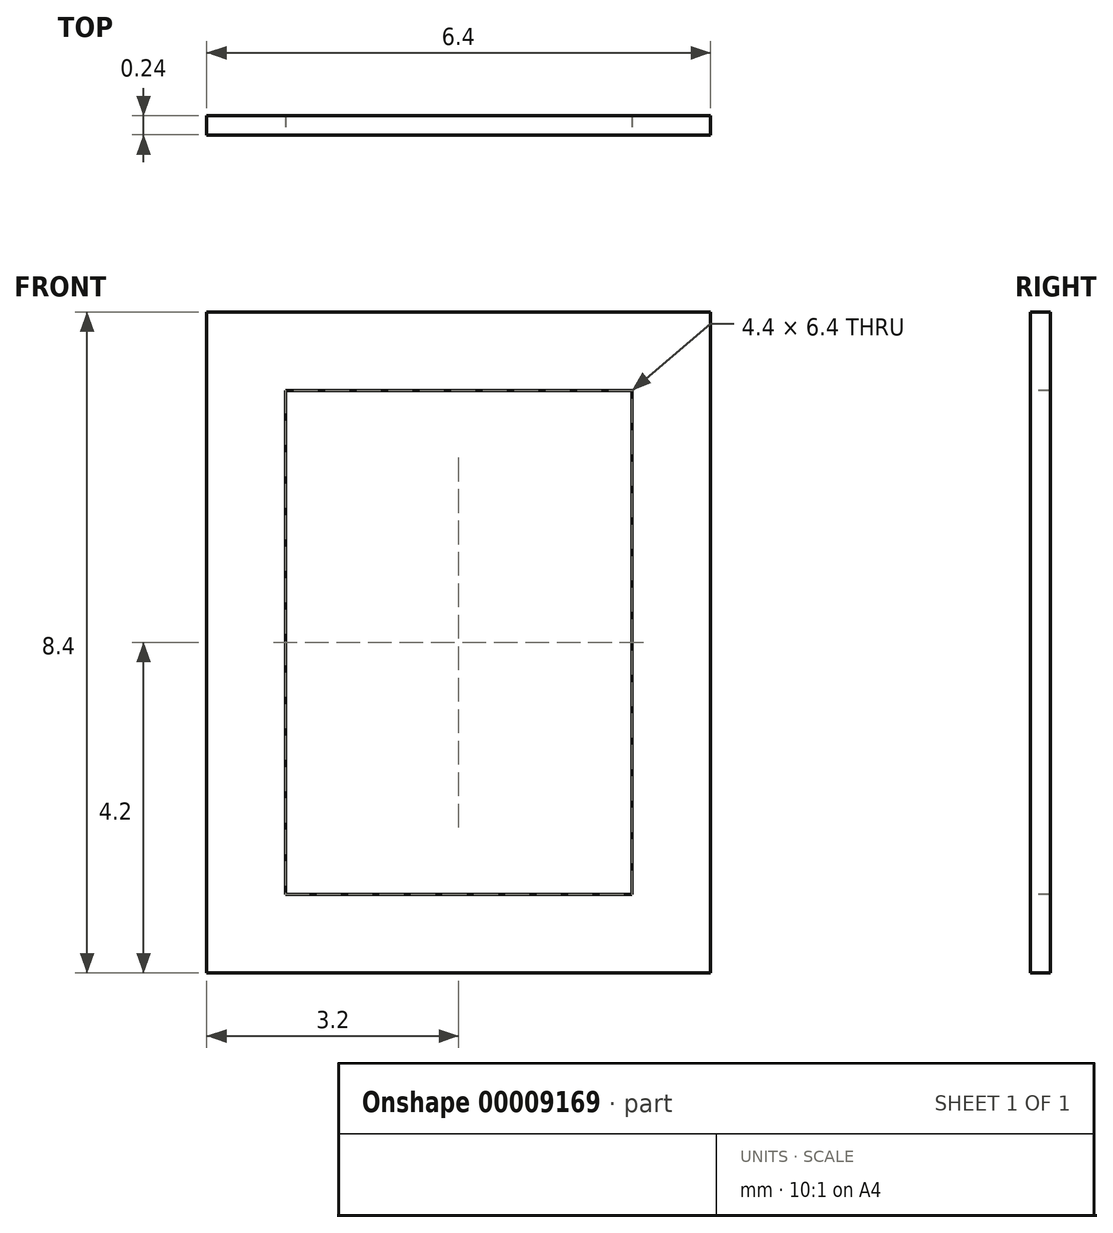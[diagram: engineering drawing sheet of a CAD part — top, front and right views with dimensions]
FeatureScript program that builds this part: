
annotation { "Feature Type Name" : "Feature", "Feature Type Description" : "" }
export const myFeature = defineFeature(function(context is Context, id is Id, definition is map)
    precondition{}
    {
        {
            var Q0;
            Q0=qCreatedBy(makeId("Top.planeOp"),FACE);
            var sketch = newSketch(context, id + "F0", { "sketchPlane" : qUnion([Q0])});
            skLineSegment(sketch, "E0.rect.bottom", {"start": v(3.2, 0.12) * mm, "end": v(-3.2, 0.13) * mm});
            skLineSegment(sketch, "E0.rect.top", {"start": v(3.2, -0.13) * mm, "end": v(-3.2, -0.12) * mm});
            skLineSegment(sketch, "E0.rect.left", {"start": v(3.2, 0.12) * mm, "end": v(3.2, -0.13) * mm});
            skLineSegment(sketch, "E0.rect.right", {"start": v(-3.2, 0.13) * mm, "end": v(-3.2, -0.12) * mm});
            skPoint(sketch, "E0.rect.middle", {"position": v(0, 0) * mm});
            skSolve(sketch);
        }
        {
            var Q0;
            Q0=makeQuery(id+"F0.imprint","IMPRINT",FACE,{"disambiguationData":[TD([[makeQuery(id+"F0.imprint","IMPRINT",EDGE,{"derivedFrom":sQuery(id+"F0.wireOp",EDGE,"E0.rect.bottom")}),1.0]])]});
            extrude(context, id + "F1", {"entities" : qUnion([Q0]), "depth" : 8.4 * mm});
        }
        {
            var Q0;
            Q0=makeQuery(id+"F1.opExtrude","SWEPT_FACE",FACE,{"disambiguationData":[OSD([sQuery(id+"F0.wireOp",EDGE,"E0.rect.top")])]});
            var sketch = newSketch(context, id + "F2", { "sketchPlane" : qUnion([Q0])});
            skLineSegment(sketch, "E1.bottom", {"start": v(-2.2, 7.4) * mm, "end": v(2.2, 7.4) * mm});
            skLineSegment(sketch, "E1.top", {"start": v(-2.2, 1) * mm, "end": v(2.2, 1) * mm});
            skLineSegment(sketch, "E1.left", {"start": v(-2.2, 7.4) * mm, "end": v(-2.2, 1) * mm});
            skLineSegment(sketch, "E1.right", {"start": v(2.2, 7.4) * mm, "end": v(2.2, 1) * mm});
            skSolve(sketch);
        }
        {
            var Q0;
            Q0=makeQuery(id+"F2.imprint","IMPRINT",FACE,{"disambiguationData":[TD([[makeQuery(id+"F2.imprint","IMPRINT",EDGE,{"derivedFrom":sQuery(id+"F2.wireOp",EDGE,"E1.bottom")}),-1.0]])]});
            extrude(context, id + "F3", {"entities" : qUnion([Q0]), "operationType" : NewBodyOperationType.REMOVE, "oppositeDirection" : true, "depth" : 25 * mm});
        }
    });
